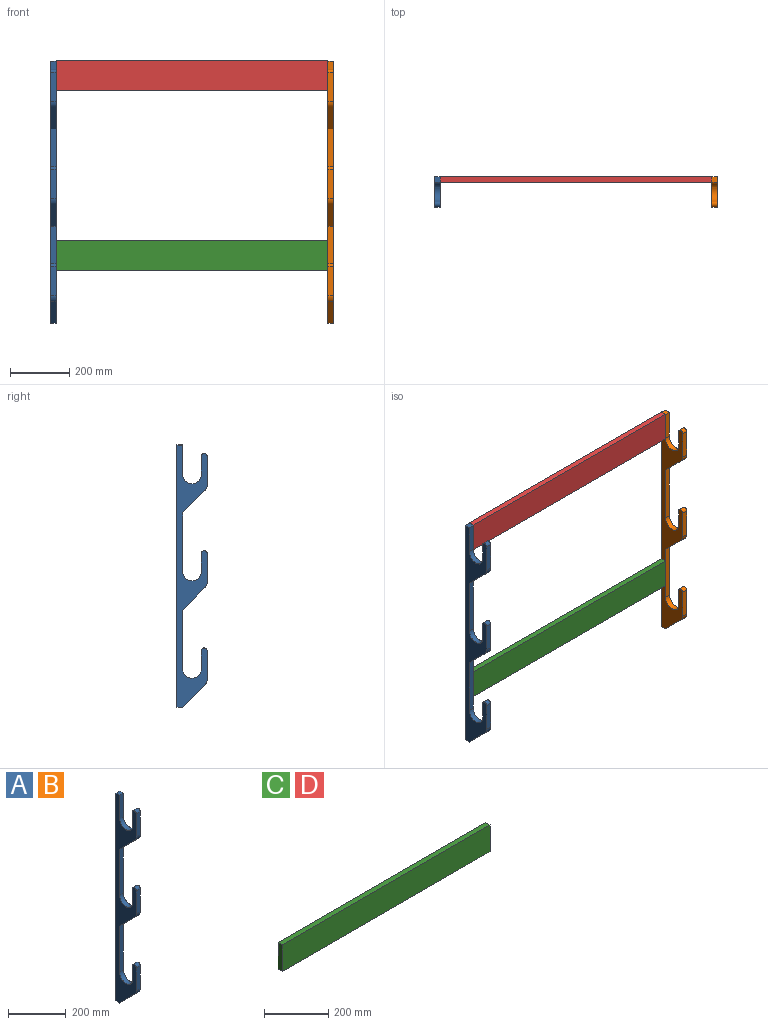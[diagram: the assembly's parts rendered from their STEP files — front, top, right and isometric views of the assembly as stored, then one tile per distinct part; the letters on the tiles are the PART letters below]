
ASSEMBLY  parts=4 mates=2
PART A: 26 faces, bbox 19.1x101.6x883.4 mm
  f0: plane 75.11x75.11mm, normal (0,-0.71,-0.71), area 2023.5mm2, adj f1,f23,f24,f25
  f1: plane 19.05x19.05mm, normal (0,0,-1), area 362.9mm2, adj f0,f2,f24,f25
  f2: plane 883.37x19.05mm, normal (0,1,0), area 16828.1mm2, adj f1,f3,f24,f25
  f3: plane 19.05x19.05mm, normal (0,0,1), area 362.9mm2, adj f2,f4,f24,f25
  f4: plane 98.07x19.05mm, normal (0,-1,0), area 1868.2mm2, adj f3,f5,f24,f25
  f5: cylinder r=31.75mm len=63.5mm, axis (-1,0,0), area 1900.2mm2, adj f4,f6,f24,f25
  f6: plane 60.33x19.05mm, normal (0,1,0), area 1149.2mm2, adj f5,f7,f24,f25
  f7: cylinder r=9.53mm len=19.05mm, axis (-1,0,0), area 570mm2, adj f6,f8,f24,f25
  f8: plane 97.79x19.05mm, normal (0,-1,0), area 1862.8mm2, adj f7,f9,f24,f25
  f9: cylinder r=25.4mm len=19.05mm, axis (-1,0,0), area 380mm2, adj f8,f10,f24,f25
  f10: plane 75.11x75.11mm, normal (0,-0.71,-0.71), area 2023.5mm2, adj f9,f11,f24,f25
  f11: plane 196.85x19.05mm, normal (0,-1,0), area 3750mm2, adj f10,f12,f24,f25
  f12: cylinder r=31.75mm len=63.5mm, axis (-1,0,0), area 1900.2mm2, adj f11,f13,f24,f25
  f13: plane 60.33x19.05mm, normal (0,1,0), area 1149.2mm2, adj f12,f14,f24,f25
  f14: cylinder r=9.53mm len=19.05mm, axis (-1,0,0), area 570mm2, adj f13,f15,f24,f25
  f15: plane 97.79x19.05mm, normal (0,-1,0), area 1862.8mm2, adj f14,f16,f24,f25
  f16: cylinder r=25.4mm len=19.05mm, axis (-1,0,0), area 380mm2, adj f15,f17,f24,f25
  f17: plane 75.11x75.11mm, normal (0,-0.71,-0.71), area 2023.5mm2, adj f16,f18,f24,f25
  f18: plane 196.85x19.05mm, normal (0,-1,0), area 3750mm2, adj f17,f19,f24,f25
  f19: cylinder r=31.75mm len=63.5mm, axis (-1,0,0), area 1900.2mm2, adj f18,f20,f24,f25
  f20: plane 60.33x19.05mm, normal (0,1,0), area 1149.2mm2, adj f19,f21,f24,f25
  f21: cylinder r=9.53mm len=19.05mm, axis (-1,0,0), area 570mm2, adj f20,f22,f24,f25
  f22: plane 97.79x19.05mm, normal (0,-1,0), area 1862.8mm2, adj f21,f23,f24,f25
  f23: cylinder r=25.4mm len=19.05mm, axis (-1,0,0), area 380mm2, adj f0,f22,f24,f25
  f24: plane 883.37x101.6mm, normal (1,0,0), area 38015.9mm2, adj f0,f1,f2,f3,f4,f5,f6,f7
  f25: plane 883.37x101.6mm, normal (-1,0,0), area 38015.9mm2, adj f0,f1,f2,f3,f4,f5,f6,f7
PART B: same geometry as A
PART C: 6 faces, bbox 914.4x19.1x101.6 mm
  f0: plane 914.4x19.05mm, normal (0,0,-1), area 17419.3mm2, adj f1,f3,f4,f5
  f1: plane 101.6x19.05mm, normal (1,0,0), area 1935.5mm2, adj f0,f2,f4,f5
  f2: plane 914.4x19.05mm, normal (0,0,1), area 17419.3mm2, adj f1,f3,f4,f5
  f3: plane 101.6x19.05mm, normal (-1,0,0), area 1935.5mm2, adj f0,f2,f4,f5
  f4: plane 914.4x101.6mm, normal (0,-1,0), area 92903mm2, adj f0,f1,f2,f3
  f5: plane 914.4x101.6mm, normal (0,1,0), area 92903mm2, adj f0,f1,f2,f3
PART D: same geometry as C
PLACE A t=(-586.87,-45.35,-101.67)mm
PLACE B t=(346.58,-45.35,-101.67)mm
PLACE C t=(-110.62,-45.35,127.29)mm fixed
PLACE D t=(-110.62,-45.35,732.66)mm
MATE fastened A.f24 <-> C.f3  axis (1,0,0) through (-567.82,-64.4,127.29)mm
MATE fastened A.f24 <-> D.f3  axis (1,0,0) through (-567.82,-64.4,732.66)mm
